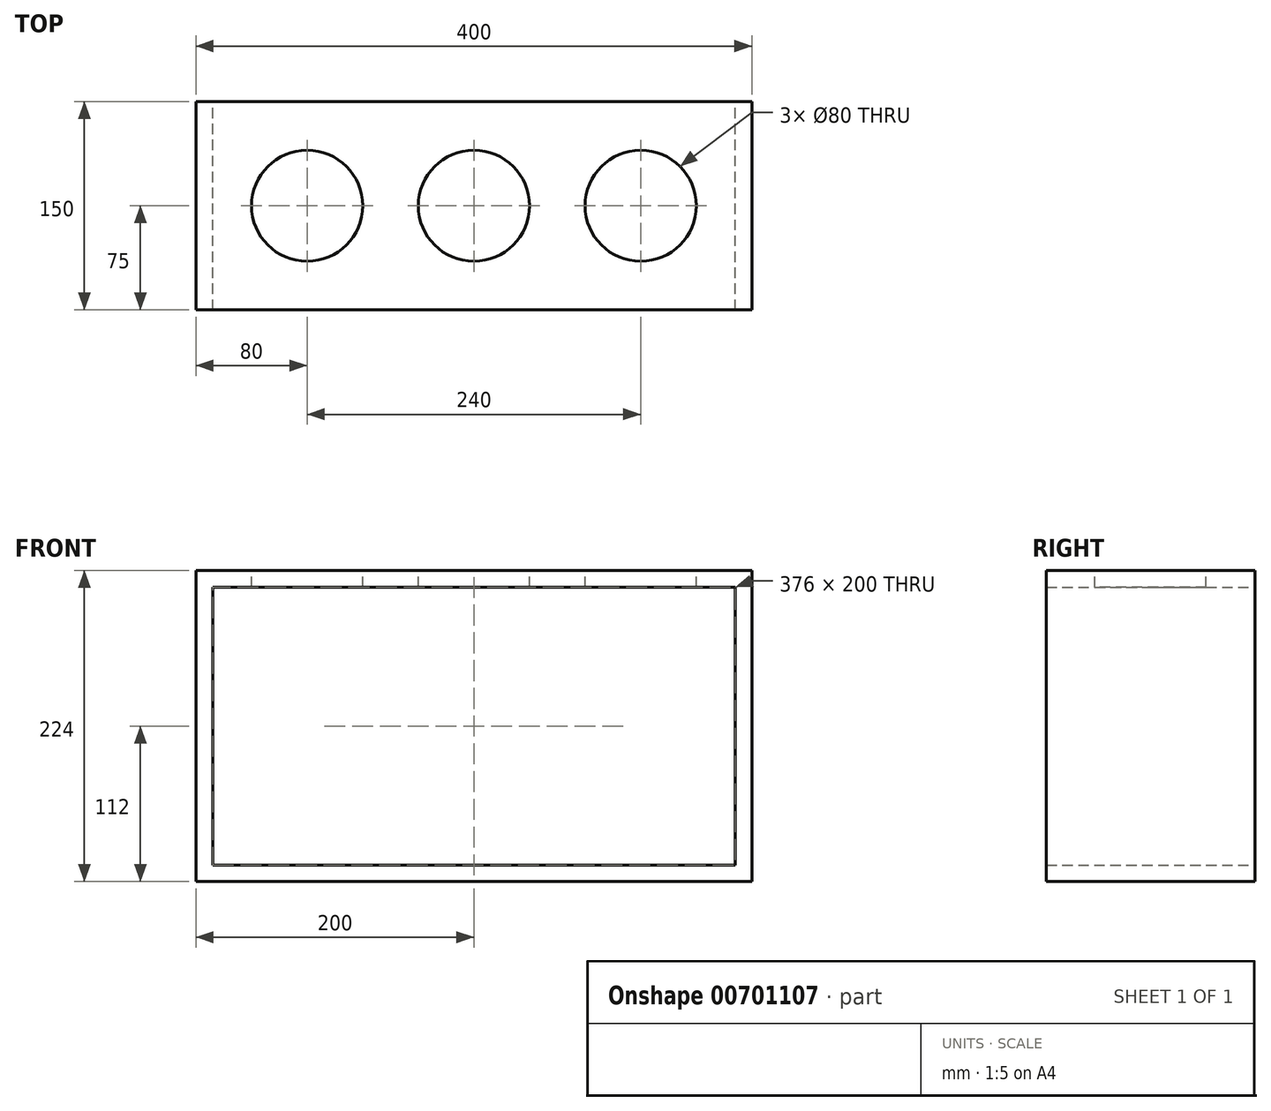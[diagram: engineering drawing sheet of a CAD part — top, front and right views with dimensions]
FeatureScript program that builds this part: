
annotation { "Feature Type Name" : "Feature", "Feature Type Description" : "" }
export const myFeature = defineFeature(function(context is Context, id is Id, definition is map)
    precondition{}
    {
        {
            var Q0;
            Q0=qCreatedBy(makeId("Top.planeOp"),FACE);
            var sketch = newSketch(context, id + "F0", { "sketchPlane" : qUnion([Q0])});
            skLineSegment(sketch, "E0.bottom", {"start": v(0, 0) * mm, "end": v(400, 0) * mm});
            skLineSegment(sketch, "E0.top", {"start": v(0, 150) * mm, "end": v(400, 150) * mm});
            skLineSegment(sketch, "E0.left", {"start": v(0, 0) * mm, "end": v(0, 150) * mm});
            skLineSegment(sketch, "E0.right", {"start": v(400, 0) * mm, "end": v(400, 150) * mm});
            skSolve(sketch);
        }
        {
            var Q0;
            Q0=makeQuery(id+"F0.imprint","IMPRINT",FACE,{"disambiguationData":[TD([[makeQuery(id+"F0.imprint","IMPRINT",EDGE,{"derivedFrom":sQuery(id+"F0.wireOp",EDGE,"E0.bottom")}),1.0]])]});
            extrude(context, id + "F1", {"entities" : qUnion([Q0]), "depth" : 12 * mm, "offsetDistance" : 25 * mm});
        }
        {
            var Q0;
            Q0=makeQuery(id+"F1.opExtrude","CAP_FACE",FACE,{"disambiguationData":[OSD([sQuery(id+"F0.wireOp",EDGE,"E0.bottom"),sQuery(id+"F0.wireOp",EDGE,"E0.top"),sQuery(id+"F0.wireOp",EDGE,"E0.left"),sQuery(id+"F0.wireOp",EDGE,"E0.right")])],"isStart":false});
            var sketch = newSketch(context, id + "F2", { "sketchPlane" : qUnion([Q0])});
            skLineSegment(sketch, "E1.bottom", {"start": v(0, 0) * mm, "end": v(12, 0) * mm});
            skLineSegment(sketch, "E1.top", {"start": v(0, 150) * mm, "end": v(12, 150) * mm});
            skLineSegment(sketch, "E1.left", {"start": v(0, 0) * mm, "end": v(0, 150) * mm});
            skLineSegment(sketch, "E1.right", {"start": v(12, 0) * mm, "end": v(12, 150) * mm});
            skSolve(sketch);
        }
        {
            var Q0;
            Q0=makeQuery(id+"F2.imprint","IMPRINT",FACE,{"disambiguationData":[TD([[makeQuery(id+"F2.imprint","IMPRINT",EDGE,{"derivedFrom":sQuery(id+"F2.wireOp",EDGE,"E1.bottom")}),1.0]])]});
            extrude(context, id + "F3", {"entities" : qUnion([Q0]), "operationType" : NewBodyOperationType.ADD, "depth" : 200 * mm, "offsetDistance" : 25 * mm});
        }
        {
            var Q0;
            Q0=makeQuery(id+"F1.opExtrude","CAP_FACE",FACE,{"disambiguationData":[OSD([sQuery(id+"F0.wireOp",EDGE,"E0.bottom"),sQuery(id+"F0.wireOp",EDGE,"E0.top"),sQuery(id+"F0.wireOp",EDGE,"E0.left"),sQuery(id+"F0.wireOp",EDGE,"E0.right")])],"isStart":false});
            var sketch = newSketch(context, id + "F4", { "sketchPlane" : qUnion([Q0])});
            skLineSegment(sketch, "E2.bottom", {"start": v(400, 0) * mm, "end": v(388, 0) * mm});
            skLineSegment(sketch, "E2.top", {"start": v(400, 150) * mm, "end": v(388, 150) * mm});
            skLineSegment(sketch, "E2.left", {"start": v(400, 0) * mm, "end": v(400, 150) * mm});
            skLineSegment(sketch, "E2.right", {"start": v(388, 0) * mm, "end": v(388, 150) * mm});
            skSolve(sketch);
        }
        {
            var Q0;
            Q0 = qSketchRegion(id + "F4", true);
            extrude(context, id + "F5", {"entities" : qUnion([Q0]), "operationType" : NewBodyOperationType.ADD, "depth" : 200 * mm, "offsetDistance" : 25 * mm});
        }
        {
            var Q0;
            Q0=makeQuery(id+"F3.opExtrude","CAP_FACE",FACE,{"disambiguationData":[OSD([sQuery(id+"F2.wireOp",EDGE,"E1.bottom"),sQuery(id+"F2.wireOp",EDGE,"E1.top"),sQuery(id+"F2.wireOp",EDGE,"E1.left"),sQuery(id+"F2.wireOp",EDGE,"E1.right")])],"isStart":false});
            var sketch = newSketch(context, id + "F6", { "sketchPlane" : qUnion([Q0])});
            skLineSegment(sketch, "E3.bottom", {"start": v(0, 0) * mm, "end": v(400, 0) * mm});
            skLineSegment(sketch, "E3.top", {"start": v(0, 150) * mm, "end": v(400, 150) * mm});
            skLineSegment(sketch, "E3.left", {"start": v(0, 0) * mm, "end": v(0, 150) * mm});
            skLineSegment(sketch, "E3.right", {"start": v(400, 0) * mm, "end": v(400, 150) * mm});
            skSolve(sketch);
        }
        {
            var Q0;
            Q0 = qSketchRegion(id + "F6", true);
            extrude(context, id + "F7", {"entities" : qUnion([Q0]), "operationType" : NewBodyOperationType.ADD, "depth" : 12 * mm, "offsetDistance" : 25 * mm});
        }
        {
            var Q0;
            Q0=makeQuery(id+"F7.opExtrude","CAP_FACE",FACE,{"disambiguationData":[OSD([sQuery(id+"F6.wireOp",EDGE,"E3.bottom"),sQuery(id+"F6.wireOp",EDGE,"E3.top"),sQuery(id+"F6.wireOp",EDGE,"E3.left"),sQuery(id+"F6.wireOp",EDGE,"E3.right")])],"isStart":false});
            var sketch = newSketch(context, id + "F8", { "sketchPlane" : qUnion([Q0])});
            skLineSegment(sketch, "E4", {"start": v(0, 75) * mm, "end": v(400, 75) * mm});
            skLineSegment(sketch, "E5", {"start": v(200, 0) * mm, "end": v(200, 150) * mm});
            skPoint(sketch, "E6", {"position": v(200, 75) * mm});
            skCircle(sketch, "E7", {"center": v(200, 75) * mm, "radius": 40 * mm});
            skPoint(sketch, "E8", {"position": v(160, 75) * mm});
            skPoint(sketch, "E9", {"position": v(240, 75) * mm});
            skPoint(sketch, "E10", {"position": v(0, 75) * mm});
            skLineSegment(sketch, "E11", {"start": v(0, 75) * mm, "end": v(80, 75) * mm});
            skCircle(sketch, "E12", {"center": v(80, 75) * mm, "radius": 40 * mm});
            skLineSegment(sketch, "E13", {"start": v(240, 75) * mm, "end": v(320, 75) * mm});
            skCircle(sketch, "E14", {"center": v(320, 75) * mm, "radius": 40 * mm});
            skSolve(sketch);
        }
        {
            var Q0;
            Q0=sQuery(id+"F8.wireOp",VERTEX,"E11.end");
            var Q1;
            Q1=makeQuery(id+"F1.opExtrude","SWEPT_BODY",BODY,{"disambiguationData":[OSD([sQuery(id+"F0.wireOp",EDGE,"E0.bottom"),sQuery(id+"F0.wireOp",EDGE,"E0.top"),sQuery(id+"F0.wireOp",EDGE,"E0.left"),sQuery(id+"F0.wireOp",EDGE,"E0.right")])]});
            hole(context, id + "F9", {"style" : HoleStyle.SIMPLE, "endStyle" : HoleEndStyle.BLIND, "holeDiameter" : 80 * mm, "majorDiameter" : 5 * mm, "holeDepth" : 12 * mm, "isTappedThrough" : true, "tappedDepth" : 12 * mm, "tapClearance" : 3, "startFromSketch" : true, "locations" : qUnion([Q0]), "scope" : qUnion([Q1])});
        }
        {
            var Q0;
            Q0=sQuery(id+"F8.wireOp",VERTEX,"E6");
            var Q1;
            Q1=makeQuery(id+"F1.opExtrude","SWEPT_BODY",BODY,{"disambiguationData":[OSD([sQuery(id+"F0.wireOp",EDGE,"E0.bottom"),sQuery(id+"F0.wireOp",EDGE,"E0.top"),sQuery(id+"F0.wireOp",EDGE,"E0.left"),sQuery(id+"F0.wireOp",EDGE,"E0.right")])]});
            hole(context, id + "F10", {"style" : HoleStyle.SIMPLE, "endStyle" : HoleEndStyle.BLIND, "holeDiameter" : 80 * mm, "majorDiameter" : 5 * mm, "holeDepth" : 12 * mm, "isTappedThrough" : true, "tappedDepth" : 12 * mm, "tapClearance" : 3, "startFromSketch" : true, "locations" : qUnion([Q0]), "scope" : qUnion([Q1])});
        }
        {
            var Q0;
            Q0=sQuery(id+"F8.wireOp",VERTEX,"E13.end");
            var Q1;
            Q1=makeQuery(id+"F1.opExtrude","SWEPT_BODY",BODY,{"disambiguationData":[OSD([sQuery(id+"F0.wireOp",EDGE,"E0.bottom"),sQuery(id+"F0.wireOp",EDGE,"E0.top"),sQuery(id+"F0.wireOp",EDGE,"E0.left"),sQuery(id+"F0.wireOp",EDGE,"E0.right")])]});
            hole(context, id + "F11", {"style" : HoleStyle.SIMPLE, "endStyle" : HoleEndStyle.BLIND, "holeDiameter" : 80 * mm, "majorDiameter" : 5 * mm, "holeDepth" : 12 * mm, "isTappedThrough" : true, "tappedDepth" : 12 * mm, "tapClearance" : 3, "startFromSketch" : true, "locations" : qUnion([Q0]), "scope" : qUnion([Q1])});
        }
    });
